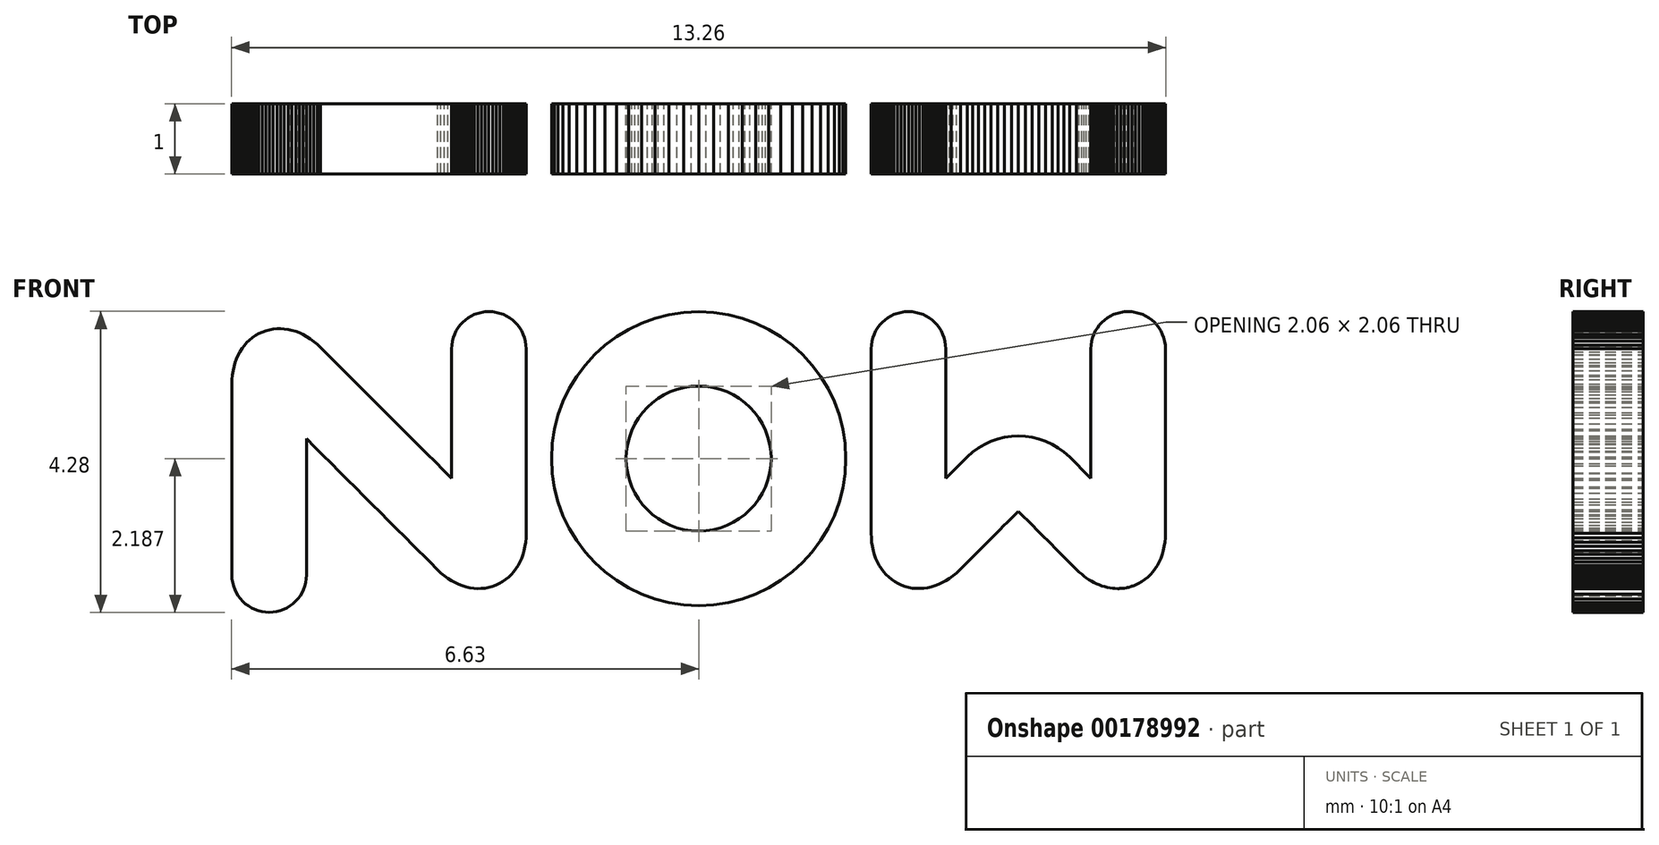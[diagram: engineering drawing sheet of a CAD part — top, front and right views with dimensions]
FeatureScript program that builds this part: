
annotation { "Feature Type Name" : "Feature", "Feature Type Description" : "" }
export const myFeature = defineFeature(function(context is Context, id is Id, definition is map)
    precondition{}
    {
        {
            var Q0;
            Q0=qCreatedBy(makeId("Front.planeOp"),FACE);
            var sketch = newSketch(context, id + "F0", { "sketchPlane" : qUnion([Q0])});
            skLineSegment(sketch, "E0", {"start": v(2.05, 0.47) * mm, "end": v(2, 0.67) * mm});
            skLineSegment(sketch, "E1", {"start": v(2, 0.67) * mm, "end": v(1.92, 0.86) * mm});
            skLineSegment(sketch, "E2", {"start": v(1.92, 0.86) * mm, "end": v(1.84, 1.04) * mm});
            skLineSegment(sketch, "E3", {"start": v(1.84, 1.04) * mm, "end": v(1.73, 1.21) * mm});
            skLineSegment(sketch, "E4", {"start": v(1.73, 1.21) * mm, "end": v(1.61, 1.37) * mm});
            skLineSegment(sketch, "E5", {"start": v(1.61, 1.37) * mm, "end": v(1.48, 1.52) * mm});
            skLineSegment(sketch, "E6", {"start": v(1.48, 1.52) * mm, "end": v(1.33, 1.66) * mm});
            skLineSegment(sketch, "E7", {"start": v(1.33, 1.66) * mm, "end": v(1.17, 1.78) * mm});
            skLineSegment(sketch, "E8", {"start": v(1.17, 1.78) * mm, "end": v(1, 1.88) * mm});
            skLineSegment(sketch, "E9", {"start": v(1, 1.88) * mm, "end": v(0.81, 1.97) * mm});
            skLineSegment(sketch, "E10", {"start": v(0.81, 1.97) * mm, "end": v(0.62, 2.04) * mm});
            skLineSegment(sketch, "E11", {"start": v(0.62, 2.04) * mm, "end": v(0.42, 2.1) * mm});
            skLineSegment(sketch, "E12", {"start": v(0.42, 2.1) * mm, "end": v(0.21, 2.12) * mm});
            skLineSegment(sketch, "E13", {"start": v(0.21, 2.12) * mm, "end": v(0, 2.14) * mm});
            skLineSegment(sketch, "E14", {"start": v(0, 2.14) * mm, "end": v(-0.21, 2.12) * mm});
            skLineSegment(sketch, "E15", {"start": v(-0.21, 2.12) * mm, "end": v(-0.42, 2.1) * mm});
            skLineSegment(sketch, "E16", {"start": v(-0.42, 2.1) * mm, "end": v(-0.62, 2.04) * mm});
            skLineSegment(sketch, "E17", {"start": v(-0.62, 2.04) * mm, "end": v(-0.81, 1.97) * mm});
            skLineSegment(sketch, "E18", {"start": v(-0.81, 1.97) * mm, "end": v(-1, 1.88) * mm});
            skLineSegment(sketch, "E19", {"start": v(-1, 1.88) * mm, "end": v(-1.17, 1.78) * mm});
            skLineSegment(sketch, "E20", {"start": v(-1.17, 1.78) * mm, "end": v(-1.33, 1.66) * mm});
            skLineSegment(sketch, "E21", {"start": v(-1.33, 1.66) * mm, "end": v(-1.48, 1.52) * mm});
            skLineSegment(sketch, "E22", {"start": v(-1.48, 1.52) * mm, "end": v(-1.61, 1.37) * mm});
            skLineSegment(sketch, "E23", {"start": v(-1.61, 1.37) * mm, "end": v(-1.73, 1.21) * mm});
            skLineSegment(sketch, "E24", {"start": v(-1.73, 1.21) * mm, "end": v(-1.84, 1.04) * mm});
            skLineSegment(sketch, "E25", {"start": v(-1.84, 1.04) * mm, "end": v(-1.92, 0.86) * mm});
            skLineSegment(sketch, "E26", {"start": v(-1.92, 0.86) * mm, "end": v(-2, 0.67) * mm});
            skLineSegment(sketch, "E27", {"start": v(-2, 0.67) * mm, "end": v(-2.05, 0.47) * mm});
            skLineSegment(sketch, "E28", {"start": v(-2.05, 0.47) * mm, "end": v(-2.08, 0.26) * mm});
            skLineSegment(sketch, "E29", {"start": v(-2.08, 0.26) * mm, "end": v(-2.09, 0.05) * mm});
            skLineSegment(sketch, "E30", {"start": v(-2.09, 0.05) * mm, "end": v(-2.08, -0.17) * mm});
            skLineSegment(sketch, "E31", {"start": v(-2.08, -0.17) * mm, "end": v(-2.05, -0.37) * mm});
            skLineSegment(sketch, "E32", {"start": v(-2.05, -0.37) * mm, "end": v(-2, -0.57) * mm});
            skLineSegment(sketch, "E33", {"start": v(-2, -0.57) * mm, "end": v(-1.92, -0.76) * mm});
            skLineSegment(sketch, "E34", {"start": v(-1.92, -0.76) * mm, "end": v(-1.84, -0.95) * mm});
            skLineSegment(sketch, "E35", {"start": v(-1.84, -0.95) * mm, "end": v(-1.73, -1.12) * mm});
            skLineSegment(sketch, "E36", {"start": v(-1.73, -1.12) * mm, "end": v(-1.61, -1.28) * mm});
            skLineSegment(sketch, "E37", {"start": v(-1.61, -1.28) * mm, "end": v(-1.48, -1.43) * mm});
            skLineSegment(sketch, "E38", {"start": v(-1.48, -1.43) * mm, "end": v(-1.33, -1.56) * mm});
            skLineSegment(sketch, "E39", {"start": v(-1.33, -1.56) * mm, "end": v(-1.17, -1.68) * mm});
            skLineSegment(sketch, "E40", {"start": v(-1.17, -1.68) * mm, "end": v(-1, -1.79) * mm});
            skLineSegment(sketch, "E41", {"start": v(-1, -1.79) * mm, "end": v(-0.81, -1.88) * mm});
            skLineSegment(sketch, "E42", {"start": v(-0.81, -1.88) * mm, "end": v(-0.62, -1.95) * mm});
            skLineSegment(sketch, "E43", {"start": v(-0.62, -1.95) * mm, "end": v(-0.42, -2) * mm});
            skLineSegment(sketch, "E44", {"start": v(-0.42, -2) * mm, "end": v(-0.21, -2.03) * mm});
            skLineSegment(sketch, "E45", {"start": v(-0.21, -2.03) * mm, "end": v(0, -2.04) * mm});
            skLineSegment(sketch, "E46", {"start": v(0, -2.04) * mm, "end": v(0.21, -2.03) * mm});
            skLineSegment(sketch, "E47", {"start": v(0.21, -2.03) * mm, "end": v(0.42, -2) * mm});
            skLineSegment(sketch, "E48", {"start": v(0.42, -2) * mm, "end": v(0.62, -1.95) * mm});
            skLineSegment(sketch, "E49", {"start": v(0.62, -1.95) * mm, "end": v(0.81, -1.88) * mm});
            skLineSegment(sketch, "E50", {"start": v(0.81, -1.88) * mm, "end": v(1, -1.79) * mm});
            skLineSegment(sketch, "E51", {"start": v(1, -1.79) * mm, "end": v(1.17, -1.68) * mm});
            skLineSegment(sketch, "E52", {"start": v(1.17, -1.68) * mm, "end": v(1.33, -1.56) * mm});
            skLineSegment(sketch, "E53", {"start": v(1.33, -1.56) * mm, "end": v(1.48, -1.43) * mm});
            skLineSegment(sketch, "E54", {"start": v(1.48, -1.43) * mm, "end": v(1.61, -1.28) * mm});
            skLineSegment(sketch, "E55", {"start": v(1.61, -1.28) * mm, "end": v(1.73, -1.12) * mm});
            skLineSegment(sketch, "E56", {"start": v(1.73, -1.12) * mm, "end": v(1.84, -0.95) * mm});
            skLineSegment(sketch, "E57", {"start": v(1.84, -0.95) * mm, "end": v(1.92, -0.76) * mm});
            skLineSegment(sketch, "E58", {"start": v(1.92, -0.76) * mm, "end": v(2, -0.57) * mm});
            skLineSegment(sketch, "E59", {"start": v(2, -0.57) * mm, "end": v(2.05, -0.37) * mm});
            skLineSegment(sketch, "E60", {"start": v(2.05, -0.37) * mm, "end": v(2.08, -0.17) * mm});
            skLineSegment(sketch, "E61", {"start": v(2.08, -0.17) * mm, "end": v(2.09, 0.05) * mm});
            skLineSegment(sketch, "E62", {"start": v(2.09, 0.05) * mm, "end": v(2.08, 0.26) * mm});
            skLineSegment(sketch, "E63", {"start": v(2.08, 0.26) * mm, "end": v(2.05, 0.47) * mm});
            skLineSegment(sketch, "E64", {"start": v(1.02, -0.06) * mm, "end": v(1, -0.16) * mm});
            skLineSegment(sketch, "E65", {"start": v(1, -0.16) * mm, "end": v(0.98, -0.26) * mm});
            skLineSegment(sketch, "E66", {"start": v(0.98, -0.26) * mm, "end": v(0.95, -0.35) * mm});
            skLineSegment(sketch, "E67", {"start": v(0.95, -0.35) * mm, "end": v(0.9, -0.44) * mm});
            skLineSegment(sketch, "E68", {"start": v(0.9, -0.44) * mm, "end": v(0.85, -0.53) * mm});
            skLineSegment(sketch, "E69", {"start": v(0.85, -0.53) * mm, "end": v(0.8, -0.6) * mm});
            skLineSegment(sketch, "E70", {"start": v(0.8, -0.6) * mm, "end": v(0.73, -0.68) * mm});
            skLineSegment(sketch, "E71", {"start": v(0.73, -0.68) * mm, "end": v(0.65, -0.75) * mm});
            skLineSegment(sketch, "E72", {"start": v(0.65, -0.75) * mm, "end": v(0.58, -0.8) * mm});
            skLineSegment(sketch, "E73", {"start": v(0.58, -0.8) * mm, "end": v(0.5, -0.86) * mm});
            skLineSegment(sketch, "E74", {"start": v(0.5, -0.86) * mm, "end": v(0.4, -0.9) * mm});
            skLineSegment(sketch, "E75", {"start": v(0.4, -0.9) * mm, "end": v(0.3, -0.94) * mm});
            skLineSegment(sketch, "E76", {"start": v(0.3, -0.94) * mm, "end": v(0.2, -0.96) * mm});
            skLineSegment(sketch, "E77", {"start": v(0.2, -0.96) * mm, "end": v(0.1, -0.98) * mm});
            skLineSegment(sketch, "E78", {"start": v(0.1, -0.98) * mm, "end": v(0, -0.98) * mm});
            skLineSegment(sketch, "E79", {"start": v(0, -0.98) * mm, "end": v(-0.1, -0.98) * mm});
            skLineSegment(sketch, "E80", {"start": v(-0.1, -0.98) * mm, "end": v(-0.2, -0.96) * mm});
            skLineSegment(sketch, "E81", {"start": v(-0.2, -0.96) * mm, "end": v(-0.3, -0.94) * mm});
            skLineSegment(sketch, "E82", {"start": v(-0.3, -0.94) * mm, "end": v(-0.4, -0.9) * mm});
            skLineSegment(sketch, "E83", {"start": v(-0.4, -0.9) * mm, "end": v(-0.5, -0.86) * mm});
            skLineSegment(sketch, "E84", {"start": v(-0.5, -0.86) * mm, "end": v(-0.58, -0.8) * mm});
            skLineSegment(sketch, "E85", {"start": v(-0.58, -0.8) * mm, "end": v(-0.65, -0.75) * mm});
            skLineSegment(sketch, "E86", {"start": v(-0.65, -0.75) * mm, "end": v(-0.73, -0.68) * mm});
            skLineSegment(sketch, "E87", {"start": v(-0.73, -0.68) * mm, "end": v(-0.8, -0.6) * mm});
            skLineSegment(sketch, "E88", {"start": v(-0.8, -0.6) * mm, "end": v(-0.85, -0.53) * mm});
            skLineSegment(sketch, "E89", {"start": v(-0.85, -0.53) * mm, "end": v(-0.9, -0.44) * mm});
            skLineSegment(sketch, "E90", {"start": v(-0.9, -0.44) * mm, "end": v(-0.95, -0.35) * mm});
            skLineSegment(sketch, "E91", {"start": v(-0.95, -0.35) * mm, "end": v(-0.98, -0.26) * mm});
            skLineSegment(sketch, "E92", {"start": v(-0.98, -0.26) * mm, "end": v(-1, -0.16) * mm});
            skLineSegment(sketch, "E93", {"start": v(-1, -0.16) * mm, "end": v(-1.02, -0.06) * mm});
            skLineSegment(sketch, "E94", {"start": v(-1.02, -0.06) * mm, "end": v(-1.03, 0.05) * mm});
            skLineSegment(sketch, "E95", {"start": v(-1.03, 0.05) * mm, "end": v(-1.02, 0.15) * mm});
            skLineSegment(sketch, "E96", {"start": v(-1.02, 0.15) * mm, "end": v(-1, 0.25) * mm});
            skLineSegment(sketch, "E97", {"start": v(-1, 0.25) * mm, "end": v(-0.98, 0.35) * mm});
            skLineSegment(sketch, "E98", {"start": v(-0.98, 0.35) * mm, "end": v(-0.95, 0.45) * mm});
            skLineSegment(sketch, "E99", {"start": v(-0.95, 0.45) * mm, "end": v(-0.9, 0.54) * mm});
            skLineSegment(sketch, "E100", {"start": v(-0.9, 0.54) * mm, "end": v(-0.85, 0.62) * mm});
            skLineSegment(sketch, "E101", {"start": v(-0.85, 0.62) * mm, "end": v(-0.8, 0.7) * mm});
            skLineSegment(sketch, "E102", {"start": v(-0.8, 0.7) * mm, "end": v(-0.73, 0.78) * mm});
            skLineSegment(sketch, "E103", {"start": v(-0.73, 0.78) * mm, "end": v(-0.65, 0.84) * mm});
            skLineSegment(sketch, "E104", {"start": v(-0.65, 0.84) * mm, "end": v(-0.58, 0.9) * mm});
            skLineSegment(sketch, "E105", {"start": v(-0.58, 0.9) * mm, "end": v(-0.5, 0.95) * mm});
            skLineSegment(sketch, "E106", {"start": v(-0.5, 0.95) * mm, "end": v(-0.4, 1) * mm});
            skLineSegment(sketch, "E107", {"start": v(-0.4, 1) * mm, "end": v(-0.3, 1.03) * mm});
            skLineSegment(sketch, "E108", {"start": v(-0.3, 1.03) * mm, "end": v(-0.2, 1.06) * mm});
            skLineSegment(sketch, "E109", {"start": v(-0.2, 1.06) * mm, "end": v(-0.1, 1.07) * mm});
            skLineSegment(sketch, "E110", {"start": v(-0.1, 1.07) * mm, "end": v(0, 1.08) * mm});
            skLineSegment(sketch, "E111", {"start": v(0, 1.08) * mm, "end": v(0.1, 1.07) * mm});
            skLineSegment(sketch, "E112", {"start": v(0.1, 1.07) * mm, "end": v(0.2, 1.06) * mm});
            skLineSegment(sketch, "E113", {"start": v(0.2, 1.06) * mm, "end": v(0.3, 1.03) * mm});
            skLineSegment(sketch, "E114", {"start": v(0.3, 1.03) * mm, "end": v(0.4, 1) * mm});
            skLineSegment(sketch, "E115", {"start": v(0.4, 1) * mm, "end": v(0.5, 0.95) * mm});
            skLineSegment(sketch, "E116", {"start": v(0.5, 0.95) * mm, "end": v(0.58, 0.9) * mm});
            skLineSegment(sketch, "E117", {"start": v(0.58, 0.9) * mm, "end": v(0.65, 0.84) * mm});
            skLineSegment(sketch, "E118", {"start": v(0.65, 0.84) * mm, "end": v(0.73, 0.78) * mm});
            skLineSegment(sketch, "E119", {"start": v(0.73, 0.78) * mm, "end": v(0.8, 0.7) * mm});
            skLineSegment(sketch, "E120", {"start": v(0.8, 0.7) * mm, "end": v(0.85, 0.62) * mm});
            skLineSegment(sketch, "E121", {"start": v(0.85, 0.62) * mm, "end": v(0.9, 0.54) * mm});
            skLineSegment(sketch, "E122", {"start": v(0.9, 0.54) * mm, "end": v(0.95, 0.45) * mm});
            skLineSegment(sketch, "E123", {"start": v(0.95, 0.45) * mm, "end": v(0.98, 0.35) * mm});
            skLineSegment(sketch, "E124", {"start": v(0.98, 0.35) * mm, "end": v(1, 0.25) * mm});
            skLineSegment(sketch, "E125", {"start": v(1, 0.25) * mm, "end": v(1.02, 0.15) * mm});
            skLineSegment(sketch, "E126", {"start": v(1.02, 0.15) * mm, "end": v(1.03, 0.05) * mm});
            skLineSegment(sketch, "E127", {"start": v(1.03, 0.05) * mm, "end": v(1.02, -0.06) * mm});
            skLineSegment(sketch, "E128", {"start": v(-2.46, 1.71) * mm, "end": v(-2.47, 1.76) * mm});
            skLineSegment(sketch, "E129", {"start": v(-2.47, 1.76) * mm, "end": v(-2.5, 1.81) * mm});
            skLineSegment(sketch, "E130", {"start": v(-2.5, 1.81) * mm, "end": v(-2.51, 1.86) * mm});
            skLineSegment(sketch, "E131", {"start": v(-2.51, 1.86) * mm, "end": v(-2.54, 1.9) * mm});
            skLineSegment(sketch, "E132", {"start": v(-2.54, 1.9) * mm, "end": v(-2.57, 1.94) * mm});
            skLineSegment(sketch, "E133", {"start": v(-2.57, 1.94) * mm, "end": v(-2.6, 1.98) * mm});
            skLineSegment(sketch, "E134", {"start": v(-2.6, 1.98) * mm, "end": v(-2.64, 2.01) * mm});
            skLineSegment(sketch, "E135", {"start": v(-2.64, 2.01) * mm, "end": v(-2.68, 2.05) * mm});
            skLineSegment(sketch, "E136", {"start": v(-2.68, 2.05) * mm, "end": v(-2.73, 2.07) * mm});
            skLineSegment(sketch, "E137", {"start": v(-2.73, 2.07) * mm, "end": v(-2.77, 2.1) * mm});
            skLineSegment(sketch, "E138", {"start": v(-2.77, 2.1) * mm, "end": v(-2.82, 2.11) * mm});
            skLineSegment(sketch, "E139", {"start": v(-2.82, 2.11) * mm, "end": v(-2.87, 2.13) * mm});
            skLineSegment(sketch, "E140", {"start": v(-2.87, 2.13) * mm, "end": v(-2.92, 2.13) * mm});
            skLineSegment(sketch, "E141", {"start": v(-2.92, 2.13) * mm, "end": v(-2.98, 2.14) * mm});
            skLineSegment(sketch, "E142", {"start": v(-2.98, 2.14) * mm, "end": v(-3.03, 2.13) * mm});
            skLineSegment(sketch, "E143", {"start": v(-3.03, 2.13) * mm, "end": v(-3.08, 2.13) * mm});
            skLineSegment(sketch, "E144", {"start": v(-3.08, 2.13) * mm, "end": v(-3.14, 2.11) * mm});
            skLineSegment(sketch, "E145", {"start": v(-3.14, 2.11) * mm, "end": v(-3.18, 2.1) * mm});
            skLineSegment(sketch, "E146", {"start": v(-3.18, 2.1) * mm, "end": v(-3.23, 2.07) * mm});
            skLineSegment(sketch, "E147", {"start": v(-3.23, 2.07) * mm, "end": v(-3.27, 2.05) * mm});
            skLineSegment(sketch, "E148", {"start": v(-3.27, 2.05) * mm, "end": v(-3.31, 2.01) * mm});
            skLineSegment(sketch, "E149", {"start": v(-3.31, 2.01) * mm, "end": v(-3.35, 1.98) * mm});
            skLineSegment(sketch, "E150", {"start": v(-3.35, 1.98) * mm, "end": v(-3.39, 1.94) * mm});
            skLineSegment(sketch, "E151", {"start": v(-3.39, 1.94) * mm, "end": v(-3.42, 1.9) * mm});
            skLineSegment(sketch, "E152", {"start": v(-3.42, 1.9) * mm, "end": v(-3.44, 1.86) * mm});
            skLineSegment(sketch, "E153", {"start": v(-3.44, 1.86) * mm, "end": v(-3.47, 1.81) * mm});
            skLineSegment(sketch, "E154", {"start": v(-3.47, 1.81) * mm, "end": v(-3.48, 1.76) * mm});
            skLineSegment(sketch, "E155", {"start": v(-3.48, 1.76) * mm, "end": v(-3.5, 1.71) * mm});
            skLineSegment(sketch, "E156", {"start": v(-3.5, 1.71) * mm, "end": v(-3.5, 1.66) * mm});
            skLineSegment(sketch, "E157", {"start": v(-3.5, 1.66) * mm, "end": v(-3.5, 1.6) * mm});
            skLineSegment(sketch, "E158", {"start": v(-3.5, 1.6) * mm, "end": v(-3.5, 1.5) * mm});
            skLineSegment(sketch, "E159", {"start": v(-3.5, 1.5) * mm, "end": v(-3.5, 1.38) * mm});
            skLineSegment(sketch, "E160", {"start": v(-3.5, 1.38) * mm, "end": v(-3.5, 1.26) * mm});
            skLineSegment(sketch, "E161", {"start": v(-3.5, 1.26) * mm, "end": v(-3.5, 1.15) * mm});
            skLineSegment(sketch, "E162", {"start": v(-3.5, 1.15) * mm, "end": v(-3.5, 1.03) * mm});
            skLineSegment(sketch, "E163", {"start": v(-3.5, 1.03) * mm, "end": v(-3.5, 0.92) * mm});
            skLineSegment(sketch, "E164", {"start": v(-3.5, 0.92) * mm, "end": v(-3.5, 0.8) * mm});
            skLineSegment(sketch, "E165", {"start": v(-3.5, 0.8) * mm, "end": v(-3.5, 0.69) * mm});
            skLineSegment(sketch, "E166", {"start": v(-3.5, 0.69) * mm, "end": v(-3.5, 0.57) * mm});
            skLineSegment(sketch, "E167", {"start": v(-3.5, 0.57) * mm, "end": v(-3.5, 0.46) * mm});
            skLineSegment(sketch, "E168", {"start": v(-3.5, 0.46) * mm, "end": v(-3.5, 0.34) * mm});
            skLineSegment(sketch, "E169", {"start": v(-3.5, 0.34) * mm, "end": v(-3.5, 0.23) * mm});
            skLineSegment(sketch, "E170", {"start": v(-3.5, 0.23) * mm, "end": v(-3.5, 0.11) * mm});
            skLineSegment(sketch, "E171", {"start": v(-3.5, 0.11) * mm, "end": v(-3.5, 0) * mm});
            skLineSegment(sketch, "E172", {"start": v(-3.5, 0) * mm, "end": v(-3.5, -0.12) * mm});
            skLineSegment(sketch, "E173", {"start": v(-3.5, -0.12) * mm, "end": v(-3.5, -0.23) * mm});
            skLineSegment(sketch, "E174", {"start": v(-3.5, -0.23) * mm, "end": v(-3.62, -0.12) * mm});
            skLineSegment(sketch, "E175", {"start": v(-3.62, -0.12) * mm, "end": v(-3.74, 0) * mm});
            skLineSegment(sketch, "E176", {"start": v(-3.74, 0) * mm, "end": v(-3.86, 0.11) * mm});
            skLineSegment(sketch, "E177", {"start": v(-3.86, 0.11) * mm, "end": v(-3.97, 0.23) * mm});
            skLineSegment(sketch, "E178", {"start": v(-3.97, 0.23) * mm, "end": v(-4.09, 0.35) * mm});
            skLineSegment(sketch, "E179", {"start": v(-4.09, 0.35) * mm, "end": v(-4.2, 0.46) * mm});
            skLineSegment(sketch, "E180", {"start": v(-4.2, 0.46) * mm, "end": v(-4.32, 0.58) * mm});
            skLineSegment(sketch, "E181", {"start": v(-4.32, 0.58) * mm, "end": v(-4.44, 0.7) * mm});
            skLineSegment(sketch, "E182", {"start": v(-4.44, 0.7) * mm, "end": v(-4.55, 0.81) * mm});
            skLineSegment(sketch, "E183", {"start": v(-4.55, 0.81) * mm, "end": v(-4.67, 0.93) * mm});
            skLineSegment(sketch, "E184", {"start": v(-4.67, 0.93) * mm, "end": v(-4.79, 1.05) * mm});
            skLineSegment(sketch, "E185", {"start": v(-4.79, 1.05) * mm, "end": v(-4.9, 1.16) * mm});
            skLineSegment(sketch, "E186", {"start": v(-4.9, 1.16) * mm, "end": v(-5.02, 1.28) * mm});
            skLineSegment(sketch, "E187", {"start": v(-5.02, 1.28) * mm, "end": v(-5.14, 1.4) * mm});
            skLineSegment(sketch, "E188", {"start": v(-5.14, 1.4) * mm, "end": v(-5.25, 1.51) * mm});
            skLineSegment(sketch, "E189", {"start": v(-5.25, 1.51) * mm, "end": v(-5.37, 1.63) * mm});
            skLineSegment(sketch, "E190", {"start": v(-5.37, 1.63) * mm, "end": v(-5.42, 1.67) * mm});
            skLineSegment(sketch, "E191", {"start": v(-5.42, 1.67) * mm, "end": v(-5.46, 1.71) * mm});
            skLineSegment(sketch, "E192", {"start": v(-5.46, 1.71) * mm, "end": v(-5.51, 1.75) * mm});
            skLineSegment(sketch, "E193", {"start": v(-5.51, 1.75) * mm, "end": v(-5.56, 1.78) * mm});
            skLineSegment(sketch, "E194", {"start": v(-5.56, 1.78) * mm, "end": v(-5.62, 1.8) * mm});
            skLineSegment(sketch, "E195", {"start": v(-5.62, 1.8) * mm, "end": v(-5.67, 1.83) * mm});
            skLineSegment(sketch, "E196", {"start": v(-5.67, 1.83) * mm, "end": v(-5.72, 1.85) * mm});
            skLineSegment(sketch, "E197", {"start": v(-5.72, 1.85) * mm, "end": v(-5.77, 1.87) * mm});
            skLineSegment(sketch, "E198", {"start": v(-5.77, 1.87) * mm, "end": v(-5.83, 1.88) * mm});
            skLineSegment(sketch, "E199", {"start": v(-5.83, 1.88) * mm, "end": v(-5.88, 1.9) * mm});
            skLineSegment(sketch, "E200", {"start": v(-5.88, 1.9) * mm, "end": v(-5.93, 1.9) * mm});
            skLineSegment(sketch, "E201", {"start": v(-5.93, 1.9) * mm, "end": v(-5.99, 1.9) * mm});
            skLineSegment(sketch, "E202", {"start": v(-5.99, 1.9) * mm, "end": v(-6.04, 1.89) * mm});
            skLineSegment(sketch, "E203", {"start": v(-6.04, 1.89) * mm, "end": v(-6.1, 1.88) * mm});
            skLineSegment(sketch, "E204", {"start": v(-6.1, 1.88) * mm, "end": v(-6.14, 1.86) * mm});
            skLineSegment(sketch, "E205", {"start": v(-6.14, 1.86) * mm, "end": v(-6.2, 1.84) * mm});
            skLineSegment(sketch, "E206", {"start": v(-6.2, 1.84) * mm, "end": v(-6.24, 1.82) * mm});
            skLineSegment(sketch, "E207", {"start": v(-6.24, 1.82) * mm, "end": v(-6.3, 1.8) * mm});
            skLineSegment(sketch, "E208", {"start": v(-6.3, 1.8) * mm, "end": v(-6.34, 1.77) * mm});
            skLineSegment(sketch, "E209", {"start": v(-6.34, 1.77) * mm, "end": v(-6.38, 1.73) * mm});
            skLineSegment(sketch, "E210", {"start": v(-6.38, 1.73) * mm, "end": v(-6.41, 1.7) * mm});
            skLineSegment(sketch, "E211", {"start": v(-6.41, 1.7) * mm, "end": v(-6.45, 1.65) * mm});
            skLineSegment(sketch, "E212", {"start": v(-6.45, 1.65) * mm, "end": v(-6.48, 1.61) * mm});
            skLineSegment(sketch, "E213", {"start": v(-6.48, 1.61) * mm, "end": v(-6.51, 1.57) * mm});
            skLineSegment(sketch, "E214", {"start": v(-6.51, 1.57) * mm, "end": v(-6.54, 1.52) * mm});
            skLineSegment(sketch, "E215", {"start": v(-6.54, 1.52) * mm, "end": v(-6.56, 1.46) * mm});
            skLineSegment(sketch, "E216", {"start": v(-6.56, 1.46) * mm, "end": v(-6.58, 1.41) * mm});
            skLineSegment(sketch, "E217", {"start": v(-6.58, 1.41) * mm, "end": v(-6.6, 1.35) * mm});
            skLineSegment(sketch, "E218", {"start": v(-6.6, 1.35) * mm, "end": v(-6.6, 1.3) * mm});
            skLineSegment(sketch, "E219", {"start": v(-6.6, 1.3) * mm, "end": v(-6.62, 1.23) * mm});
            skLineSegment(sketch, "E220", {"start": v(-6.62, 1.23) * mm, "end": v(-6.62, 1.17) * mm});
            skLineSegment(sketch, "E221", {"start": v(-6.62, 1.17) * mm, "end": v(-6.63, 1.1) * mm});
            skLineSegment(sketch, "E222", {"start": v(-6.63, 1.1) * mm, "end": v(-6.63, 0.94) * mm});
            skLineSegment(sketch, "E223", {"start": v(-6.63, 0.94) * mm, "end": v(-6.63, 0.77) * mm});
            skLineSegment(sketch, "E224", {"start": v(-6.63, 0.77) * mm, "end": v(-6.63, 0.6) * mm});
            skLineSegment(sketch, "E225", {"start": v(-6.63, 0.6) * mm, "end": v(-6.63, 0.43) * mm});
            skLineSegment(sketch, "E226", {"start": v(-6.63, 0.43) * mm, "end": v(-6.63, 0.26) * mm});
            skLineSegment(sketch, "E227", {"start": v(-6.63, 0.26) * mm, "end": v(-6.63, 0.09) * mm});
            skLineSegment(sketch, "E228", {"start": v(-6.63, 0.09) * mm, "end": v(-6.63, -0.08) * mm});
            skLineSegment(sketch, "E229", {"start": v(-6.63, -0.08) * mm, "end": v(-6.63, -0.25) * mm});
            skLineSegment(sketch, "E230", {"start": v(-6.63, -0.25) * mm, "end": v(-6.63, -0.42) * mm});
            skLineSegment(sketch, "E231", {"start": v(-6.63, -0.42) * mm, "end": v(-6.63, -0.59) * mm});
            skLineSegment(sketch, "E232", {"start": v(-6.63, -0.59) * mm, "end": v(-6.63, -0.76) * mm});
            skLineSegment(sketch, "E233", {"start": v(-6.63, -0.76) * mm, "end": v(-6.63, -0.93) * mm});
            skLineSegment(sketch, "E234", {"start": v(-6.63, -0.93) * mm, "end": v(-6.63, -1.1) * mm});
            skLineSegment(sketch, "E235", {"start": v(-6.63, -1.1) * mm, "end": v(-6.63, -1.27) * mm});
            skLineSegment(sketch, "E236", {"start": v(-6.63, -1.27) * mm, "end": v(-6.63, -1.44) * mm});
            skLineSegment(sketch, "E237", {"start": v(-6.63, -1.44) * mm, "end": v(-6.63, -1.6) * mm});
            skLineSegment(sketch, "E238", {"start": v(-6.63, -1.6) * mm, "end": v(-6.62, -1.66) * mm});
            skLineSegment(sketch, "E239", {"start": v(-6.62, -1.66) * mm, "end": v(-6.62, -1.71) * mm});
            skLineSegment(sketch, "E240", {"start": v(-6.62, -1.71) * mm, "end": v(-6.6, -1.76) * mm});
            skLineSegment(sketch, "E241", {"start": v(-6.6, -1.76) * mm, "end": v(-6.58, -1.81) * mm});
            skLineSegment(sketch, "E242", {"start": v(-6.58, -1.81) * mm, "end": v(-6.56, -1.86) * mm});
            skLineSegment(sketch, "E243", {"start": v(-6.56, -1.86) * mm, "end": v(-6.54, -1.9) * mm});
            skLineSegment(sketch, "E244", {"start": v(-6.54, -1.9) * mm, "end": v(-6.5, -1.94) * mm});
            skLineSegment(sketch, "E245", {"start": v(-6.5, -1.94) * mm, "end": v(-6.47, -1.98) * mm});
            skLineSegment(sketch, "E246", {"start": v(-6.47, -1.98) * mm, "end": v(-6.43, -2.02) * mm});
            skLineSegment(sketch, "E247", {"start": v(-6.43, -2.02) * mm, "end": v(-6.4, -2.05) * mm});
            skLineSegment(sketch, "E248", {"start": v(-6.4, -2.05) * mm, "end": v(-6.35, -2.07) * mm});
            skLineSegment(sketch, "E249", {"start": v(-6.35, -2.07) * mm, "end": v(-6.3, -2.1) * mm});
            skLineSegment(sketch, "E250", {"start": v(-6.3, -2.1) * mm, "end": v(-6.25, -2.11) * mm});
            skLineSegment(sketch, "E251", {"start": v(-6.25, -2.11) * mm, "end": v(-6.2, -2.13) * mm});
            skLineSegment(sketch, "E252", {"start": v(-6.2, -2.13) * mm, "end": v(-6.15, -2.13) * mm});
            skLineSegment(sketch, "E253", {"start": v(-6.15, -2.13) * mm, "end": v(-6.1, -2.14) * mm});
            skLineSegment(sketch, "E254", {"start": v(-6.1, -2.14) * mm, "end": v(-6.04, -2.13) * mm});
            skLineSegment(sketch, "E255", {"start": v(-6.04, -2.13) * mm, "end": v(-6, -2.13) * mm});
            skLineSegment(sketch, "E256", {"start": v(-6, -2.13) * mm, "end": v(-5.94, -2.11) * mm});
            skLineSegment(sketch, "E257", {"start": v(-5.94, -2.11) * mm, "end": v(-5.9, -2.1) * mm});
            skLineSegment(sketch, "E258", {"start": v(-5.9, -2.1) * mm, "end": v(-5.84, -2.07) * mm});
            skLineSegment(sketch, "E259", {"start": v(-5.84, -2.07) * mm, "end": v(-5.8, -2.05) * mm});
            skLineSegment(sketch, "E260", {"start": v(-5.8, -2.05) * mm, "end": v(-5.76, -2.02) * mm});
            skLineSegment(sketch, "E261", {"start": v(-5.76, -2.02) * mm, "end": v(-5.72, -1.98) * mm});
            skLineSegment(sketch, "E262", {"start": v(-5.72, -1.98) * mm, "end": v(-5.69, -1.94) * mm});
            skLineSegment(sketch, "E263", {"start": v(-5.69, -1.94) * mm, "end": v(-5.66, -1.9) * mm});
            skLineSegment(sketch, "E264", {"start": v(-5.66, -1.9) * mm, "end": v(-5.63, -1.86) * mm});
            skLineSegment(sketch, "E265", {"start": v(-5.63, -1.86) * mm, "end": v(-5.6, -1.81) * mm});
            skLineSegment(sketch, "E266", {"start": v(-5.6, -1.81) * mm, "end": v(-5.6, -1.76) * mm});
            skLineSegment(sketch, "E267", {"start": v(-5.6, -1.76) * mm, "end": v(-5.58, -1.71) * mm});
            skLineSegment(sketch, "E268", {"start": v(-5.58, -1.71) * mm, "end": v(-5.57, -1.66) * mm});
            skLineSegment(sketch, "E269", {"start": v(-5.57, -1.66) * mm, "end": v(-5.57, -1.6) * mm});
            skLineSegment(sketch, "E270", {"start": v(-5.57, -1.6) * mm, "end": v(-5.57, -1.49) * mm});
            skLineSegment(sketch, "E271", {"start": v(-5.57, -1.49) * mm, "end": v(-5.57, -1.36) * mm});
            skLineSegment(sketch, "E272", {"start": v(-5.57, -1.36) * mm, "end": v(-5.57, -1.24) * mm});
            skLineSegment(sketch, "E273", {"start": v(-5.57, -1.24) * mm, "end": v(-5.57, -1.12) * mm});
            skLineSegment(sketch, "E274", {"start": v(-5.57, -1.12) * mm, "end": v(-5.57, -1) * mm});
            skLineSegment(sketch, "E275", {"start": v(-5.57, -1) * mm, "end": v(-5.57, -0.88) * mm});
            skLineSegment(sketch, "E276", {"start": v(-5.57, -0.88) * mm, "end": v(-5.57, -0.76) * mm});
            skLineSegment(sketch, "E277", {"start": v(-5.57, -0.76) * mm, "end": v(-5.57, -0.64) * mm});
            skLineSegment(sketch, "E278", {"start": v(-5.57, -0.64) * mm, "end": v(-5.57, -0.52) * mm});
            skLineSegment(sketch, "E279", {"start": v(-5.57, -0.52) * mm, "end": v(-5.57, -0.4) * mm});
            skLineSegment(sketch, "E280", {"start": v(-5.57, -0.4) * mm, "end": v(-5.57, -0.28) * mm});
            skLineSegment(sketch, "E281", {"start": v(-5.57, -0.28) * mm, "end": v(-5.57, -0.15) * mm});
            skLineSegment(sketch, "E282", {"start": v(-5.57, -0.15) * mm, "end": v(-5.57, -0.03) * mm});
            skLineSegment(sketch, "E283", {"start": v(-5.57, -0.03) * mm, "end": v(-5.57, 0.09) * mm});
            skLineSegment(sketch, "E284", {"start": v(-5.57, 0.09) * mm, "end": v(-5.57, 0.2) * mm});
            skLineSegment(sketch, "E285", {"start": v(-5.57, 0.2) * mm, "end": v(-5.57, 0.33) * mm});
            skLineSegment(sketch, "E286", {"start": v(-5.57, 0.33) * mm, "end": v(-5.45, 0.21) * mm});
            skLineSegment(sketch, "E287", {"start": v(-5.45, 0.21) * mm, "end": v(-5.33, 0.1) * mm});
            skLineSegment(sketch, "E288", {"start": v(-5.33, 0.1) * mm, "end": v(-5.22, -0.02) * mm});
            skLineSegment(sketch, "E289", {"start": v(-5.22, -0.02) * mm, "end": v(-5.1, -0.14) * mm});
            skLineSegment(sketch, "E290", {"start": v(-5.1, -0.14) * mm, "end": v(-4.99, -0.25) * mm});
            skLineSegment(sketch, "E291", {"start": v(-4.99, -0.25) * mm, "end": v(-4.87, -0.37) * mm});
            skLineSegment(sketch, "E292", {"start": v(-4.87, -0.37) * mm, "end": v(-4.75, -0.49) * mm});
            skLineSegment(sketch, "E293", {"start": v(-4.75, -0.49) * mm, "end": v(-4.64, -0.6) * mm});
            skLineSegment(sketch, "E294", {"start": v(-4.64, -0.6) * mm, "end": v(-4.52, -0.72) * mm});
            skLineSegment(sketch, "E295", {"start": v(-4.52, -0.72) * mm, "end": v(-4.4, -0.83) * mm});
            skLineSegment(sketch, "E296", {"start": v(-4.4, -0.83) * mm, "end": v(-4.29, -0.95) * mm});
            skLineSegment(sketch, "E297", {"start": v(-4.29, -0.95) * mm, "end": v(-4.17, -1.07) * mm});
            skLineSegment(sketch, "E298", {"start": v(-4.17, -1.07) * mm, "end": v(-4.05, -1.18) * mm});
            skLineSegment(sketch, "E299", {"start": v(-4.05, -1.18) * mm, "end": v(-3.94, -1.3) * mm});
            skLineSegment(sketch, "E300", {"start": v(-3.94, -1.3) * mm, "end": v(-3.82, -1.42) * mm});
            skLineSegment(sketch, "E301", {"start": v(-3.82, -1.42) * mm, "end": v(-3.7, -1.53) * mm});
            skLineSegment(sketch, "E302", {"start": v(-3.7, -1.53) * mm, "end": v(-3.66, -1.58) * mm});
            skLineSegment(sketch, "E303", {"start": v(-3.66, -1.58) * mm, "end": v(-3.61, -1.62) * mm});
            skLineSegment(sketch, "E304", {"start": v(-3.61, -1.62) * mm, "end": v(-3.56, -1.65) * mm});
            skLineSegment(sketch, "E305", {"start": v(-3.56, -1.65) * mm, "end": v(-3.51, -1.69) * mm});
            skLineSegment(sketch, "E306", {"start": v(-3.51, -1.69) * mm, "end": v(-3.46, -1.72) * mm});
            skLineSegment(sketch, "E307", {"start": v(-3.46, -1.72) * mm, "end": v(-3.4, -1.74) * mm});
            skLineSegment(sketch, "E308", {"start": v(-3.4, -1.74) * mm, "end": v(-3.35, -1.76) * mm});
            skLineSegment(sketch, "E309", {"start": v(-3.35, -1.76) * mm, "end": v(-3.3, -1.78) * mm});
            skLineSegment(sketch, "E310", {"start": v(-3.3, -1.78) * mm, "end": v(-3.25, -1.79) * mm});
            skLineSegment(sketch, "E311", {"start": v(-3.25, -1.79) * mm, "end": v(-3.2, -1.8) * mm});
            skLineSegment(sketch, "E312", {"start": v(-3.2, -1.8) * mm, "end": v(-3.14, -1.8) * mm});
            skLineSegment(sketch, "E313", {"start": v(-3.14, -1.8) * mm, "end": v(-3.09, -1.8) * mm});
            skLineSegment(sketch, "E314", {"start": v(-3.09, -1.8) * mm, "end": v(-3.03, -1.8) * mm});
            skLineSegment(sketch, "E315", {"start": v(-3.03, -1.8) * mm, "end": v(-2.98, -1.78) * mm});
            skLineSegment(sketch, "E316", {"start": v(-2.98, -1.78) * mm, "end": v(-2.93, -1.77) * mm});
            skLineSegment(sketch, "E317", {"start": v(-2.93, -1.77) * mm, "end": v(-2.88, -1.75) * mm});
            skLineSegment(sketch, "E318", {"start": v(-2.88, -1.75) * mm, "end": v(-2.83, -1.73) * mm});
            skLineSegment(sketch, "E319", {"start": v(-2.83, -1.73) * mm, "end": v(-2.78, -1.7) * mm});
            skLineSegment(sketch, "E320", {"start": v(-2.78, -1.7) * mm, "end": v(-2.74, -1.67) * mm});
            skLineSegment(sketch, "E321", {"start": v(-2.74, -1.67) * mm, "end": v(-2.7, -1.64) * mm});
            skLineSegment(sketch, "E322", {"start": v(-2.7, -1.64) * mm, "end": v(-2.66, -1.6) * mm});
            skLineSegment(sketch, "E323", {"start": v(-2.66, -1.6) * mm, "end": v(-2.62, -1.56) * mm});
            skLineSegment(sketch, "E324", {"start": v(-2.62, -1.56) * mm, "end": v(-2.6, -1.52) * mm});
            skLineSegment(sketch, "E325", {"start": v(-2.6, -1.52) * mm, "end": v(-2.56, -1.47) * mm});
            skLineSegment(sketch, "E326", {"start": v(-2.56, -1.47) * mm, "end": v(-2.54, -1.42) * mm});
            skLineSegment(sketch, "E327", {"start": v(-2.54, -1.42) * mm, "end": v(-2.51, -1.37) * mm});
            skLineSegment(sketch, "E328", {"start": v(-2.51, -1.37) * mm, "end": v(-2.5, -1.32) * mm});
            skLineSegment(sketch, "E329", {"start": v(-2.5, -1.32) * mm, "end": v(-2.48, -1.26) * mm});
            skLineSegment(sketch, "E330", {"start": v(-2.48, -1.26) * mm, "end": v(-2.47, -1.2) * mm});
            skLineSegment(sketch, "E331", {"start": v(-2.47, -1.2) * mm, "end": v(-2.46, -1.14) * mm});
            skLineSegment(sketch, "E332", {"start": v(-2.46, -1.14) * mm, "end": v(-2.45, -1.08) * mm});
            skLineSegment(sketch, "E333", {"start": v(-2.45, -1.08) * mm, "end": v(-2.45, -1.01) * mm});
            skLineSegment(sketch, "E334", {"start": v(-2.45, -1.01) * mm, "end": v(-2.45, -0.85) * mm});
            skLineSegment(sketch, "E335", {"start": v(-2.45, -0.85) * mm, "end": v(-2.45, -0.68) * mm});
            skLineSegment(sketch, "E336", {"start": v(-2.45, -0.68) * mm, "end": v(-2.45, -0.52) * mm});
            skLineSegment(sketch, "E337", {"start": v(-2.45, -0.52) * mm, "end": v(-2.45, -0.36) * mm});
            skLineSegment(sketch, "E338", {"start": v(-2.45, -0.36) * mm, "end": v(-2.45, -0.2) * mm});
            skLineSegment(sketch, "E339", {"start": v(-2.45, -0.2) * mm, "end": v(-2.45, -0.03) * mm});
            skLineSegment(sketch, "E340", {"start": v(-2.45, -0.03) * mm, "end": v(-2.45, 0.13) * mm});
            skLineSegment(sketch, "E341", {"start": v(-2.45, 0.13) * mm, "end": v(-2.45, 0.3) * mm});
            skLineSegment(sketch, "E342", {"start": v(-2.45, 0.3) * mm, "end": v(-2.45, 0.46) * mm});
            skLineSegment(sketch, "E343", {"start": v(-2.45, 0.46) * mm, "end": v(-2.45, 0.62) * mm});
            skLineSegment(sketch, "E344", {"start": v(-2.45, 0.62) * mm, "end": v(-2.45, 0.79) * mm});
            skLineSegment(sketch, "E345", {"start": v(-2.45, 0.79) * mm, "end": v(-2.45, 0.95) * mm});
            skLineSegment(sketch, "E346", {"start": v(-2.45, 0.95) * mm, "end": v(-2.45, 1.12) * mm});
            skLineSegment(sketch, "E347", {"start": v(-2.45, 1.12) * mm, "end": v(-2.45, 1.28) * mm});
            skLineSegment(sketch, "E348", {"start": v(-2.45, 1.28) * mm, "end": v(-2.45, 1.44) * mm});
            skLineSegment(sketch, "E349", {"start": v(-2.45, 1.44) * mm, "end": v(-2.45, 1.6) * mm});
            skLineSegment(sketch, "E350", {"start": v(-2.45, 1.6) * mm, "end": v(-2.45, 1.66) * mm});
            skLineSegment(sketch, "E351", {"start": v(-2.45, 1.66) * mm, "end": v(-2.46, 1.71) * mm});
            skLineSegment(sketch, "E352", {"start": v(6.62, 1.66) * mm, "end": v(6.62, 1.71) * mm});
            skLineSegment(sketch, "E353", {"start": v(6.62, 1.71) * mm, "end": v(6.6, 1.76) * mm});
            skLineSegment(sketch, "E354", {"start": v(6.6, 1.76) * mm, "end": v(6.58, 1.81) * mm});
            skLineSegment(sketch, "E355", {"start": v(6.58, 1.81) * mm, "end": v(6.56, 1.86) * mm});
            skLineSegment(sketch, "E356", {"start": v(6.56, 1.86) * mm, "end": v(6.54, 1.9) * mm});
            skLineSegment(sketch, "E357", {"start": v(6.54, 1.9) * mm, "end": v(6.5, 1.94) * mm});
            skLineSegment(sketch, "E358", {"start": v(6.5, 1.94) * mm, "end": v(6.47, 1.98) * mm});
            skLineSegment(sketch, "E359", {"start": v(6.47, 1.98) * mm, "end": v(6.43, 2.01) * mm});
            skLineSegment(sketch, "E360", {"start": v(6.43, 2.01) * mm, "end": v(6.4, 2.05) * mm});
            skLineSegment(sketch, "E361", {"start": v(6.4, 2.05) * mm, "end": v(6.35, 2.07) * mm});
            skLineSegment(sketch, "E362", {"start": v(6.35, 2.07) * mm, "end": v(6.3, 2.1) * mm});
            skLineSegment(sketch, "E363", {"start": v(6.3, 2.1) * mm, "end": v(6.25, 2.11) * mm});
            skLineSegment(sketch, "E364", {"start": v(6.25, 2.11) * mm, "end": v(6.2, 2.13) * mm});
            skLineSegment(sketch, "E365", {"start": v(6.2, 2.13) * mm, "end": v(6.15, 2.13) * mm});
            skLineSegment(sketch, "E366", {"start": v(6.15, 2.13) * mm, "end": v(6.1, 2.14) * mm});
            skLineSegment(sketch, "E367", {"start": v(6.1, 2.14) * mm, "end": v(6.04, 2.13) * mm});
            skLineSegment(sketch, "E368", {"start": v(6.04, 2.13) * mm, "end": v(5.99, 2.13) * mm});
            skLineSegment(sketch, "E369", {"start": v(5.99, 2.13) * mm, "end": v(5.94, 2.11) * mm});
            skLineSegment(sketch, "E370", {"start": v(5.94, 2.11) * mm, "end": v(5.9, 2.1) * mm});
            skLineSegment(sketch, "E371", {"start": v(5.9, 2.1) * mm, "end": v(5.84, 2.07) * mm});
            skLineSegment(sketch, "E372", {"start": v(5.84, 2.07) * mm, "end": v(5.8, 2.05) * mm});
            skLineSegment(sketch, "E373", {"start": v(5.8, 2.05) * mm, "end": v(5.76, 2.01) * mm});
            skLineSegment(sketch, "E374", {"start": v(5.76, 2.01) * mm, "end": v(5.72, 1.98) * mm});
            skLineSegment(sketch, "E375", {"start": v(5.72, 1.98) * mm, "end": v(5.69, 1.94) * mm});
            skLineSegment(sketch, "E376", {"start": v(5.69, 1.94) * mm, "end": v(5.66, 1.9) * mm});
            skLineSegment(sketch, "E377", {"start": v(5.66, 1.9) * mm, "end": v(5.63, 1.86) * mm});
            skLineSegment(sketch, "E378", {"start": v(5.63, 1.86) * mm, "end": v(5.6, 1.81) * mm});
            skLineSegment(sketch, "E379", {"start": v(5.6, 1.81) * mm, "end": v(5.6, 1.76) * mm});
            skLineSegment(sketch, "E380", {"start": v(5.6, 1.76) * mm, "end": v(5.58, 1.71) * mm});
            skLineSegment(sketch, "E381", {"start": v(5.58, 1.71) * mm, "end": v(5.57, 1.66) * mm});
            skLineSegment(sketch, "E382", {"start": v(5.57, 1.66) * mm, "end": v(5.57, 1.6) * mm});
            skLineSegment(sketch, "E383", {"start": v(5.57, 1.6) * mm, "end": v(5.57, 1.5) * mm});
            skLineSegment(sketch, "E384", {"start": v(5.57, 1.5) * mm, "end": v(5.57, 1.38) * mm});
            skLineSegment(sketch, "E385", {"start": v(5.57, 1.38) * mm, "end": v(5.57, 1.26) * mm});
            skLineSegment(sketch, "E386", {"start": v(5.57, 1.26) * mm, "end": v(5.57, 1.15) * mm});
            skLineSegment(sketch, "E387", {"start": v(5.57, 1.15) * mm, "end": v(5.57, 1.03) * mm});
            skLineSegment(sketch, "E388", {"start": v(5.57, 1.03) * mm, "end": v(5.57, 0.92) * mm});
            skLineSegment(sketch, "E389", {"start": v(5.57, 0.92) * mm, "end": v(5.57, 0.8) * mm});
            skLineSegment(sketch, "E390", {"start": v(5.57, 0.8) * mm, "end": v(5.57, 0.69) * mm});
            skLineSegment(sketch, "E391", {"start": v(5.57, 0.69) * mm, "end": v(5.57, 0.57) * mm});
            skLineSegment(sketch, "E392", {"start": v(5.57, 0.57) * mm, "end": v(5.57, 0.46) * mm});
            skLineSegment(sketch, "E393", {"start": v(5.57, 0.46) * mm, "end": v(5.57, 0.34) * mm});
            skLineSegment(sketch, "E394", {"start": v(5.57, 0.34) * mm, "end": v(5.57, 0.23) * mm});
            skLineSegment(sketch, "E395", {"start": v(5.57, 0.23) * mm, "end": v(5.57, 0.11) * mm});
            skLineSegment(sketch, "E396", {"start": v(5.57, 0.11) * mm, "end": v(5.57, 0) * mm});
            skLineSegment(sketch, "E397", {"start": v(5.57, 0) * mm, "end": v(5.57, -0.12) * mm});
            skLineSegment(sketch, "E398", {"start": v(5.57, -0.12) * mm, "end": v(5.57, -0.23) * mm});
            skLineSegment(sketch, "E399", {"start": v(5.57, -0.23) * mm, "end": v(5.55, -0.22) * mm});
            skLineSegment(sketch, "E400", {"start": v(5.55, -0.22) * mm, "end": v(5.53, -0.2) * mm});
            skLineSegment(sketch, "E401", {"start": v(5.53, -0.2) * mm, "end": v(5.51, -0.18) * mm});
            skLineSegment(sketch, "E402", {"start": v(5.51, -0.18) * mm, "end": v(5.5, -0.16) * mm});
            skLineSegment(sketch, "E403", {"start": v(5.5, -0.16) * mm, "end": v(5.47, -0.14) * mm});
            skLineSegment(sketch, "E404", {"start": v(5.47, -0.14) * mm, "end": v(5.45, -0.12) * mm});
            skLineSegment(sketch, "E405", {"start": v(5.45, -0.12) * mm, "end": v(5.44, -0.1) * mm});
            skLineSegment(sketch, "E406", {"start": v(5.44, -0.1) * mm, "end": v(5.42, -0.08) * mm});
            skLineSegment(sketch, "E407", {"start": v(5.42, -0.08) * mm, "end": v(5.4, -0.06) * mm});
            skLineSegment(sketch, "E408", {"start": v(5.4, -0.06) * mm, "end": v(5.38, -0.05) * mm});
            skLineSegment(sketch, "E409", {"start": v(5.38, -0.05) * mm, "end": v(5.36, -0.03) * mm});
            skLineSegment(sketch, "E410", {"start": v(5.36, -0.03) * mm, "end": v(5.34, 0) * mm});
            skLineSegment(sketch, "E411", {"start": v(5.34, 0) * mm, "end": v(5.32, 0.01) * mm});
            skLineSegment(sketch, "E412", {"start": v(5.32, 0.01) * mm, "end": v(5.3, 0.03) * mm});
            skLineSegment(sketch, "E413", {"start": v(5.3, 0.03) * mm, "end": v(5.28, 0.05) * mm});
            skLineSegment(sketch, "E414", {"start": v(5.28, 0.05) * mm, "end": v(5.27, 0.07) * mm});
            skLineSegment(sketch, "E415", {"start": v(5.27, 0.07) * mm, "end": v(5.19, 0.14) * mm});
            skLineSegment(sketch, "E416", {"start": v(5.19, 0.14) * mm, "end": v(5.1, 0.2) * mm});
            skLineSegment(sketch, "E417", {"start": v(5.1, 0.2) * mm, "end": v(5.02, 0.25) * mm});
            skLineSegment(sketch, "E418", {"start": v(5.02, 0.25) * mm, "end": v(4.92, 0.3) * mm});
            skLineSegment(sketch, "E419", {"start": v(4.92, 0.3) * mm, "end": v(4.83, 0.33) * mm});
            skLineSegment(sketch, "E420", {"start": v(4.83, 0.33) * mm, "end": v(4.73, 0.35) * mm});
            skLineSegment(sketch, "E421", {"start": v(4.73, 0.35) * mm, "end": v(4.64, 0.36) * mm});
            skLineSegment(sketch, "E422", {"start": v(4.64, 0.36) * mm, "end": v(4.54, 0.37) * mm});
            skLineSegment(sketch, "E423", {"start": v(4.54, 0.37) * mm, "end": v(4.44, 0.36) * mm});
            skLineSegment(sketch, "E424", {"start": v(4.44, 0.36) * mm, "end": v(4.34, 0.35) * mm});
            skLineSegment(sketch, "E425", {"start": v(4.34, 0.35) * mm, "end": v(4.24, 0.33) * mm});
            skLineSegment(sketch, "E426", {"start": v(4.24, 0.33) * mm, "end": v(4.15, 0.3) * mm});
            skLineSegment(sketch, "E427", {"start": v(4.15, 0.3) * mm, "end": v(4.06, 0.25) * mm});
            skLineSegment(sketch, "E428", {"start": v(4.06, 0.25) * mm, "end": v(3.97, 0.2) * mm});
            skLineSegment(sketch, "E429", {"start": v(3.97, 0.2) * mm, "end": v(3.89, 0.14) * mm});
            skLineSegment(sketch, "E430", {"start": v(3.89, 0.14) * mm, "end": v(3.8, 0.07) * mm});
            skLineSegment(sketch, "E431", {"start": v(3.8, 0.07) * mm, "end": v(3.8, 0.05) * mm});
            skLineSegment(sketch, "E432", {"start": v(3.8, 0.05) * mm, "end": v(3.77, 0.03) * mm});
            skLineSegment(sketch, "E433", {"start": v(3.77, 0.03) * mm, "end": v(3.75, 0.01) * mm});
            skLineSegment(sketch, "E434", {"start": v(3.75, 0.01) * mm, "end": v(3.73, 0) * mm});
            skLineSegment(sketch, "E435", {"start": v(3.73, 0) * mm, "end": v(3.72, -0.03) * mm});
            skLineSegment(sketch, "E436", {"start": v(3.72, -0.03) * mm, "end": v(3.7, -0.05) * mm});
            skLineSegment(sketch, "E437", {"start": v(3.7, -0.05) * mm, "end": v(3.68, -0.06) * mm});
            skLineSegment(sketch, "E438", {"start": v(3.68, -0.06) * mm, "end": v(3.66, -0.08) * mm});
            skLineSegment(sketch, "E439", {"start": v(3.66, -0.08) * mm, "end": v(3.64, -0.1) * mm});
            skLineSegment(sketch, "E440", {"start": v(3.64, -0.1) * mm, "end": v(3.62, -0.12) * mm});
            skLineSegment(sketch, "E441", {"start": v(3.62, -0.12) * mm, "end": v(3.6, -0.14) * mm});
            skLineSegment(sketch, "E442", {"start": v(3.6, -0.14) * mm, "end": v(3.58, -0.16) * mm});
            skLineSegment(sketch, "E443", {"start": v(3.58, -0.16) * mm, "end": v(3.56, -0.18) * mm});
            skLineSegment(sketch, "E444", {"start": v(3.56, -0.18) * mm, "end": v(3.55, -0.2) * mm});
            skLineSegment(sketch, "E445", {"start": v(3.55, -0.2) * mm, "end": v(3.53, -0.22) * mm});
            skLineSegment(sketch, "E446", {"start": v(3.53, -0.22) * mm, "end": v(3.5, -0.23) * mm});
            skLineSegment(sketch, "E447", {"start": v(3.5, -0.23) * mm, "end": v(3.5, -0.12) * mm});
            skLineSegment(sketch, "E448", {"start": v(3.5, -0.12) * mm, "end": v(3.5, 0) * mm});
            skLineSegment(sketch, "E449", {"start": v(3.5, 0) * mm, "end": v(3.5, 0.11) * mm});
            skLineSegment(sketch, "E450", {"start": v(3.5, 0.11) * mm, "end": v(3.5, 0.23) * mm});
            skLineSegment(sketch, "E451", {"start": v(3.5, 0.23) * mm, "end": v(3.5, 0.34) * mm});
            skLineSegment(sketch, "E452", {"start": v(3.5, 0.34) * mm, "end": v(3.5, 0.46) * mm});
            skLineSegment(sketch, "E453", {"start": v(3.5, 0.46) * mm, "end": v(3.5, 0.57) * mm});
            skLineSegment(sketch, "E454", {"start": v(3.5, 0.57) * mm, "end": v(3.5, 0.69) * mm});
            skLineSegment(sketch, "E455", {"start": v(3.5, 0.69) * mm, "end": v(3.5, 0.8) * mm});
            skLineSegment(sketch, "E456", {"start": v(3.5, 0.8) * mm, "end": v(3.5, 0.92) * mm});
            skLineSegment(sketch, "E457", {"start": v(3.5, 0.92) * mm, "end": v(3.5, 1.03) * mm});
            skLineSegment(sketch, "E458", {"start": v(3.5, 1.03) * mm, "end": v(3.5, 1.15) * mm});
            skLineSegment(sketch, "E459", {"start": v(3.5, 1.15) * mm, "end": v(3.5, 1.26) * mm});
            skLineSegment(sketch, "E460", {"start": v(3.5, 1.26) * mm, "end": v(3.5, 1.38) * mm});
            skLineSegment(sketch, "E461", {"start": v(3.5, 1.38) * mm, "end": v(3.5, 1.5) * mm});
            skLineSegment(sketch, "E462", {"start": v(3.5, 1.5) * mm, "end": v(3.5, 1.6) * mm});
            skLineSegment(sketch, "E463", {"start": v(3.5, 1.6) * mm, "end": v(3.5, 1.66) * mm});
            skLineSegment(sketch, "E464", {"start": v(3.5, 1.66) * mm, "end": v(3.5, 1.71) * mm});
            skLineSegment(sketch, "E465", {"start": v(3.5, 1.71) * mm, "end": v(3.48, 1.76) * mm});
            skLineSegment(sketch, "E466", {"start": v(3.48, 1.76) * mm, "end": v(3.47, 1.81) * mm});
            skLineSegment(sketch, "E467", {"start": v(3.47, 1.81) * mm, "end": v(3.44, 1.86) * mm});
            skLineSegment(sketch, "E468", {"start": v(3.44, 1.86) * mm, "end": v(3.42, 1.9) * mm});
            skLineSegment(sketch, "E469", {"start": v(3.42, 1.9) * mm, "end": v(3.39, 1.94) * mm});
            skLineSegment(sketch, "E470", {"start": v(3.39, 1.94) * mm, "end": v(3.35, 1.98) * mm});
            skLineSegment(sketch, "E471", {"start": v(3.35, 1.98) * mm, "end": v(3.31, 2.01) * mm});
            skLineSegment(sketch, "E472", {"start": v(3.31, 2.01) * mm, "end": v(3.27, 2.05) * mm});
            skLineSegment(sketch, "E473", {"start": v(3.27, 2.05) * mm, "end": v(3.23, 2.07) * mm});
            skLineSegment(sketch, "E474", {"start": v(3.23, 2.07) * mm, "end": v(3.18, 2.1) * mm});
            skLineSegment(sketch, "E475", {"start": v(3.18, 2.1) * mm, "end": v(3.14, 2.11) * mm});
            skLineSegment(sketch, "E476", {"start": v(3.14, 2.11) * mm, "end": v(3.09, 2.13) * mm});
            skLineSegment(sketch, "E477", {"start": v(3.09, 2.13) * mm, "end": v(3.03, 2.13) * mm});
            skLineSegment(sketch, "E478", {"start": v(3.03, 2.13) * mm, "end": v(2.98, 2.14) * mm});
            skLineSegment(sketch, "E479", {"start": v(2.98, 2.14) * mm, "end": v(2.92, 2.13) * mm});
            skLineSegment(sketch, "E480", {"start": v(2.92, 2.13) * mm, "end": v(2.87, 2.13) * mm});
            skLineSegment(sketch, "E481", {"start": v(2.87, 2.13) * mm, "end": v(2.82, 2.11) * mm});
            skLineSegment(sketch, "E482", {"start": v(2.82, 2.11) * mm, "end": v(2.77, 2.1) * mm});
            skLineSegment(sketch, "E483", {"start": v(2.77, 2.1) * mm, "end": v(2.73, 2.07) * mm});
            skLineSegment(sketch, "E484", {"start": v(2.73, 2.07) * mm, "end": v(2.68, 2.05) * mm});
            skLineSegment(sketch, "E485", {"start": v(2.68, 2.05) * mm, "end": v(2.64, 2.01) * mm});
            skLineSegment(sketch, "E486", {"start": v(2.64, 2.01) * mm, "end": v(2.6, 1.98) * mm});
            skLineSegment(sketch, "E487", {"start": v(2.6, 1.98) * mm, "end": v(2.57, 1.94) * mm});
            skLineSegment(sketch, "E488", {"start": v(2.57, 1.94) * mm, "end": v(2.54, 1.9) * mm});
            skLineSegment(sketch, "E489", {"start": v(2.54, 1.9) * mm, "end": v(2.51, 1.86) * mm});
            skLineSegment(sketch, "E490", {"start": v(2.51, 1.86) * mm, "end": v(2.5, 1.81) * mm});
            skLineSegment(sketch, "E491", {"start": v(2.5, 1.81) * mm, "end": v(2.47, 1.76) * mm});
            skLineSegment(sketch, "E492", {"start": v(2.47, 1.76) * mm, "end": v(2.46, 1.71) * mm});
            skLineSegment(sketch, "E493", {"start": v(2.46, 1.71) * mm, "end": v(2.45, 1.66) * mm});
            skLineSegment(sketch, "E494", {"start": v(2.45, 1.66) * mm, "end": v(2.45, 1.6) * mm});
            skLineSegment(sketch, "E495", {"start": v(2.45, 1.6) * mm, "end": v(2.45, 1.44) * mm});
            skLineSegment(sketch, "E496", {"start": v(2.45, 1.44) * mm, "end": v(2.45, 1.28) * mm});
            skLineSegment(sketch, "E497", {"start": v(2.45, 1.28) * mm, "end": v(2.45, 1.12) * mm});
            skLineSegment(sketch, "E498", {"start": v(2.45, 1.12) * mm, "end": v(2.45, 0.95) * mm});
            skLineSegment(sketch, "E499", {"start": v(2.45, 0.95) * mm, "end": v(2.45, 0.79) * mm});
            skLineSegment(sketch, "E500", {"start": v(2.45, 0.79) * mm, "end": v(2.45, 0.62) * mm});
            skLineSegment(sketch, "E501", {"start": v(2.45, 0.62) * mm, "end": v(2.45, 0.46) * mm});
            skLineSegment(sketch, "E502", {"start": v(2.45, 0.46) * mm, "end": v(2.45, 0.3) * mm});
            skLineSegment(sketch, "E503", {"start": v(2.45, 0.3) * mm, "end": v(2.45, 0.13) * mm});
            skLineSegment(sketch, "E504", {"start": v(2.45, 0.13) * mm, "end": v(2.45, -0.03) * mm});
            skLineSegment(sketch, "E505", {"start": v(2.45, -0.03) * mm, "end": v(2.45, -0.2) * mm});
            skLineSegment(sketch, "E506", {"start": v(2.45, -0.2) * mm, "end": v(2.45, -0.36) * mm});
            skLineSegment(sketch, "E507", {"start": v(2.45, -0.36) * mm, "end": v(2.45, -0.52) * mm});
            skLineSegment(sketch, "E508", {"start": v(2.45, -0.52) * mm, "end": v(2.45, -0.68) * mm});
            skLineSegment(sketch, "E509", {"start": v(2.45, -0.68) * mm, "end": v(2.45, -0.85) * mm});
            skLineSegment(sketch, "E510", {"start": v(2.45, -0.85) * mm, "end": v(2.45, -1.01) * mm});
            skLineSegment(sketch, "E511", {"start": v(2.45, -1.01) * mm, "end": v(2.45, -1.08) * mm});
            skLineSegment(sketch, "E512", {"start": v(2.45, -1.08) * mm, "end": v(2.46, -1.14) * mm});
            skLineSegment(sketch, "E513", {"start": v(2.46, -1.14) * mm, "end": v(2.47, -1.2) * mm});
            skLineSegment(sketch, "E514", {"start": v(2.47, -1.2) * mm, "end": v(2.48, -1.26) * mm});
            skLineSegment(sketch, "E515", {"start": v(2.48, -1.26) * mm, "end": v(2.5, -1.32) * mm});
            skLineSegment(sketch, "E516", {"start": v(2.5, -1.32) * mm, "end": v(2.51, -1.37) * mm});
            skLineSegment(sketch, "E517", {"start": v(2.51, -1.37) * mm, "end": v(2.54, -1.42) * mm});
            skLineSegment(sketch, "E518", {"start": v(2.54, -1.42) * mm, "end": v(2.56, -1.47) * mm});
            skLineSegment(sketch, "E519", {"start": v(2.56, -1.47) * mm, "end": v(2.6, -1.52) * mm});
            skLineSegment(sketch, "E520", {"start": v(2.6, -1.52) * mm, "end": v(2.62, -1.56) * mm});
            skLineSegment(sketch, "E521", {"start": v(2.62, -1.56) * mm, "end": v(2.66, -1.6) * mm});
            skLineSegment(sketch, "E522", {"start": v(2.66, -1.6) * mm, "end": v(2.7, -1.64) * mm});
            skLineSegment(sketch, "E523", {"start": v(2.7, -1.64) * mm, "end": v(2.74, -1.67) * mm});
            skLineSegment(sketch, "E524", {"start": v(2.74, -1.67) * mm, "end": v(2.78, -1.7) * mm});
            skLineSegment(sketch, "E525", {"start": v(2.78, -1.7) * mm, "end": v(2.83, -1.73) * mm});
            skLineSegment(sketch, "E526", {"start": v(2.83, -1.73) * mm, "end": v(2.88, -1.75) * mm});
            skLineSegment(sketch, "E527", {"start": v(2.88, -1.75) * mm, "end": v(2.93, -1.77) * mm});
            skLineSegment(sketch, "E528", {"start": v(2.93, -1.77) * mm, "end": v(2.98, -1.78) * mm});
            skLineSegment(sketch, "E529", {"start": v(2.98, -1.78) * mm, "end": v(3.03, -1.8) * mm});
            skLineSegment(sketch, "E530", {"start": v(3.03, -1.8) * mm, "end": v(3.09, -1.8) * mm});
            skLineSegment(sketch, "E531", {"start": v(3.09, -1.8) * mm, "end": v(3.14, -1.8) * mm});
            skLineSegment(sketch, "E532", {"start": v(3.14, -1.8) * mm, "end": v(3.2, -1.8) * mm});
            skLineSegment(sketch, "E533", {"start": v(3.2, -1.8) * mm, "end": v(3.25, -1.79) * mm});
            skLineSegment(sketch, "E534", {"start": v(3.25, -1.79) * mm, "end": v(3.3, -1.78) * mm});
            skLineSegment(sketch, "E535", {"start": v(3.3, -1.78) * mm, "end": v(3.35, -1.76) * mm});
            skLineSegment(sketch, "E536", {"start": v(3.35, -1.76) * mm, "end": v(3.4, -1.74) * mm});
            skLineSegment(sketch, "E537", {"start": v(3.4, -1.74) * mm, "end": v(3.46, -1.72) * mm});
            skLineSegment(sketch, "E538", {"start": v(3.46, -1.72) * mm, "end": v(3.51, -1.69) * mm});
            skLineSegment(sketch, "E539", {"start": v(3.51, -1.69) * mm, "end": v(3.56, -1.65) * mm});
            skLineSegment(sketch, "E540", {"start": v(3.56, -1.65) * mm, "end": v(3.61, -1.62) * mm});
            skLineSegment(sketch, "E541", {"start": v(3.61, -1.62) * mm, "end": v(3.66, -1.58) * mm});
            skLineSegment(sketch, "E542", {"start": v(3.66, -1.58) * mm, "end": v(3.7, -1.53) * mm});
            skLineSegment(sketch, "E543", {"start": v(3.7, -1.53) * mm, "end": v(3.76, -1.48) * mm});
            skLineSegment(sketch, "E544", {"start": v(3.76, -1.48) * mm, "end": v(3.8, -1.43) * mm});
            skLineSegment(sketch, "E545", {"start": v(3.8, -1.43) * mm, "end": v(3.86, -1.38) * mm});
            skLineSegment(sketch, "E546", {"start": v(3.86, -1.38) * mm, "end": v(3.91, -1.32) * mm});
            skLineSegment(sketch, "E547", {"start": v(3.91, -1.32) * mm, "end": v(3.97, -1.27) * mm});
            skLineSegment(sketch, "E548", {"start": v(3.97, -1.27) * mm, "end": v(4.02, -1.22) * mm});
            skLineSegment(sketch, "E549", {"start": v(4.02, -1.22) * mm, "end": v(4.07, -1.17) * mm});
            skLineSegment(sketch, "E550", {"start": v(4.07, -1.17) * mm, "end": v(4.12, -1.12) * mm});
            skLineSegment(sketch, "E551", {"start": v(4.12, -1.12) * mm, "end": v(4.17, -1.06) * mm});
            skLineSegment(sketch, "E552", {"start": v(4.17, -1.06) * mm, "end": v(4.23, -1.01) * mm});
            skLineSegment(sketch, "E553", {"start": v(4.23, -1.01) * mm, "end": v(4.28, -0.96) * mm});
            skLineSegment(sketch, "E554", {"start": v(4.28, -0.96) * mm, "end": v(4.33, -0.9) * mm});
            skLineSegment(sketch, "E555", {"start": v(4.33, -0.9) * mm, "end": v(4.38, -0.86) * mm});
            skLineSegment(sketch, "E556", {"start": v(4.38, -0.86) * mm, "end": v(4.43, -0.8) * mm});
            skLineSegment(sketch, "E557", {"start": v(4.43, -0.8) * mm, "end": v(4.49, -0.75) * mm});
            skLineSegment(sketch, "E558", {"start": v(4.49, -0.75) * mm, "end": v(4.54, -0.7) * mm});
            skLineSegment(sketch, "E559", {"start": v(4.54, -0.7) * mm, "end": v(4.59, -0.75) * mm});
            skLineSegment(sketch, "E560", {"start": v(4.59, -0.75) * mm, "end": v(4.64, -0.8) * mm});
            skLineSegment(sketch, "E561", {"start": v(4.64, -0.8) * mm, "end": v(4.7, -0.86) * mm});
            skLineSegment(sketch, "E562", {"start": v(4.7, -0.86) * mm, "end": v(4.75, -0.9) * mm});
            skLineSegment(sketch, "E563", {"start": v(4.75, -0.9) * mm, "end": v(4.8, -0.96) * mm});
            skLineSegment(sketch, "E564", {"start": v(4.8, -0.96) * mm, "end": v(4.85, -1.01) * mm});
            skLineSegment(sketch, "E565", {"start": v(4.85, -1.01) * mm, "end": v(4.9, -1.06) * mm});
            skLineSegment(sketch, "E566", {"start": v(4.9, -1.06) * mm, "end": v(4.95, -1.12) * mm});
            skLineSegment(sketch, "E567", {"start": v(4.95, -1.12) * mm, "end": v(5, -1.17) * mm});
            skLineSegment(sketch, "E568", {"start": v(5, -1.17) * mm, "end": v(5.06, -1.22) * mm});
            skLineSegment(sketch, "E569", {"start": v(5.06, -1.22) * mm, "end": v(5.1, -1.27) * mm});
            skLineSegment(sketch, "E570", {"start": v(5.1, -1.27) * mm, "end": v(5.16, -1.32) * mm});
            skLineSegment(sketch, "E571", {"start": v(5.16, -1.32) * mm, "end": v(5.21, -1.38) * mm});
            skLineSegment(sketch, "E572", {"start": v(5.21, -1.38) * mm, "end": v(5.27, -1.43) * mm});
            skLineSegment(sketch, "E573", {"start": v(5.27, -1.43) * mm, "end": v(5.32, -1.48) * mm});
            skLineSegment(sketch, "E574", {"start": v(5.32, -1.48) * mm, "end": v(5.37, -1.53) * mm});
            skLineSegment(sketch, "E575", {"start": v(5.37, -1.53) * mm, "end": v(5.4, -1.56) * mm});
            skLineSegment(sketch, "E576", {"start": v(5.4, -1.56) * mm, "end": v(5.44, -1.6) * mm});
            skLineSegment(sketch, "E577", {"start": v(5.44, -1.6) * mm, "end": v(5.47, -1.62) * mm});
            skLineSegment(sketch, "E578", {"start": v(5.47, -1.62) * mm, "end": v(5.5, -1.65) * mm});
            skLineSegment(sketch, "E579", {"start": v(5.5, -1.65) * mm, "end": v(5.54, -1.67) * mm});
            skLineSegment(sketch, "E580", {"start": v(5.54, -1.67) * mm, "end": v(5.58, -1.7) * mm});
            skLineSegment(sketch, "E581", {"start": v(5.58, -1.7) * mm, "end": v(5.61, -1.71) * mm});
            skLineSegment(sketch, "E582", {"start": v(5.61, -1.71) * mm, "end": v(5.65, -1.73) * mm});
            skLineSegment(sketch, "E583", {"start": v(5.65, -1.73) * mm, "end": v(5.69, -1.75) * mm});
            skLineSegment(sketch, "E584", {"start": v(5.69, -1.75) * mm, "end": v(5.72, -1.76) * mm});
            skLineSegment(sketch, "E585", {"start": v(5.72, -1.76) * mm, "end": v(5.76, -1.77) * mm});
            skLineSegment(sketch, "E586", {"start": v(5.76, -1.77) * mm, "end": v(5.8, -1.78) * mm});
            skLineSegment(sketch, "E587", {"start": v(5.8, -1.78) * mm, "end": v(5.84, -1.79) * mm});
            skLineSegment(sketch, "E588", {"start": v(5.84, -1.79) * mm, "end": v(5.87, -1.8) * mm});
            skLineSegment(sketch, "E589", {"start": v(5.87, -1.8) * mm, "end": v(5.91, -1.8) * mm});
            skLineSegment(sketch, "E590", {"start": v(5.91, -1.8) * mm, "end": v(5.95, -1.8) * mm});
            skLineSegment(sketch, "E591", {"start": v(5.95, -1.8) * mm, "end": v(5.96, -1.8) * mm});
            skLineSegment(sketch, "E592", {"start": v(5.96, -1.8) * mm, "end": v(5.98, -1.8) * mm});
            skLineSegment(sketch, "E593", {"start": v(5.98, -1.8) * mm, "end": v(6, -1.8) * mm});
            skLineSegment(sketch, "E594", {"start": v(6, -1.8) * mm, "end": v(6.01, -1.8) * mm});
            skLineSegment(sketch, "E595", {"start": v(6.01, -1.8) * mm, "end": v(6.03, -1.8) * mm});
            skLineSegment(sketch, "E596", {"start": v(6.03, -1.8) * mm, "end": v(6.04, -1.8) * mm});
            skLineSegment(sketch, "E597", {"start": v(6.04, -1.8) * mm, "end": v(6.06, -1.79) * mm});
            skLineSegment(sketch, "E598", {"start": v(6.06, -1.79) * mm, "end": v(6.07, -1.79) * mm});
            skLineSegment(sketch, "E599", {"start": v(6.07, -1.79) * mm, "end": v(6.09, -1.78) * mm});
            skLineSegment(sketch, "E600", {"start": v(6.09, -1.78) * mm, "end": v(6.1, -1.78) * mm});
            skLineSegment(sketch, "E601", {"start": v(6.1, -1.78) * mm, "end": v(6.12, -1.78) * mm});
            skLineSegment(sketch, "E602", {"start": v(6.12, -1.78) * mm, "end": v(6.14, -1.77) * mm});
            skLineSegment(sketch, "E603", {"start": v(6.14, -1.77) * mm, "end": v(6.15, -1.77) * mm});
            skLineSegment(sketch, "E604", {"start": v(6.15, -1.77) * mm, "end": v(6.17, -1.76) * mm});
            skLineSegment(sketch, "E605", {"start": v(6.17, -1.76) * mm, "end": v(6.18, -1.76) * mm});
            skLineSegment(sketch, "E606", {"start": v(6.18, -1.76) * mm, "end": v(6.2, -1.75) * mm});
            skLineSegment(sketch, "E607", {"start": v(6.2, -1.75) * mm, "end": v(6.24, -1.73) * mm});
            skLineSegment(sketch, "E608", {"start": v(6.24, -1.73) * mm, "end": v(6.3, -1.7) * mm});
            skLineSegment(sketch, "E609", {"start": v(6.3, -1.7) * mm, "end": v(6.34, -1.67) * mm});
            skLineSegment(sketch, "E610", {"start": v(6.34, -1.67) * mm, "end": v(6.38, -1.64) * mm});
            skLineSegment(sketch, "E611", {"start": v(6.38, -1.64) * mm, "end": v(6.41, -1.6) * mm});
            skLineSegment(sketch, "E612", {"start": v(6.41, -1.6) * mm, "end": v(6.45, -1.56) * mm});
            skLineSegment(sketch, "E613", {"start": v(6.45, -1.56) * mm, "end": v(6.48, -1.52) * mm});
            skLineSegment(sketch, "E614", {"start": v(6.48, -1.52) * mm, "end": v(6.51, -1.47) * mm});
            skLineSegment(sketch, "E615", {"start": v(6.51, -1.47) * mm, "end": v(6.54, -1.42) * mm});
            skLineSegment(sketch, "E616", {"start": v(6.54, -1.42) * mm, "end": v(6.56, -1.37) * mm});
            skLineSegment(sketch, "E617", {"start": v(6.56, -1.37) * mm, "end": v(6.58, -1.32) * mm});
            skLineSegment(sketch, "E618", {"start": v(6.58, -1.32) * mm, "end": v(6.6, -1.26) * mm});
            skLineSegment(sketch, "E619", {"start": v(6.6, -1.26) * mm, "end": v(6.6, -1.2) * mm});
            skLineSegment(sketch, "E620", {"start": v(6.6, -1.2) * mm, "end": v(6.62, -1.14) * mm});
            skLineSegment(sketch, "E621", {"start": v(6.62, -1.14) * mm, "end": v(6.62, -1.08) * mm});
            skLineSegment(sketch, "E622", {"start": v(6.62, -1.08) * mm, "end": v(6.63, -1.01) * mm});
            skLineSegment(sketch, "E623", {"start": v(6.63, -1.01) * mm, "end": v(6.63, -0.85) * mm});
            skLineSegment(sketch, "E624", {"start": v(6.63, -0.85) * mm, "end": v(6.63, -0.68) * mm});
            skLineSegment(sketch, "E625", {"start": v(6.63, -0.68) * mm, "end": v(6.63, -0.52) * mm});
            skLineSegment(sketch, "E626", {"start": v(6.63, -0.52) * mm, "end": v(6.63, -0.36) * mm});
            skLineSegment(sketch, "E627", {"start": v(6.63, -0.36) * mm, "end": v(6.63, -0.2) * mm});
            skLineSegment(sketch, "E628", {"start": v(6.63, -0.2) * mm, "end": v(6.63, -0.03) * mm});
            skLineSegment(sketch, "E629", {"start": v(6.63, -0.03) * mm, "end": v(6.63, 0.13) * mm});
            skLineSegment(sketch, "E630", {"start": v(6.63, 0.13) * mm, "end": v(6.63, 0.3) * mm});
            skLineSegment(sketch, "E631", {"start": v(6.63, 0.3) * mm, "end": v(6.63, 0.46) * mm});
            skLineSegment(sketch, "E632", {"start": v(6.63, 0.46) * mm, "end": v(6.63, 0.62) * mm});
            skLineSegment(sketch, "E633", {"start": v(6.63, 0.62) * mm, "end": v(6.63, 0.79) * mm});
            skLineSegment(sketch, "E634", {"start": v(6.63, 0.79) * mm, "end": v(6.63, 0.95) * mm});
            skLineSegment(sketch, "E635", {"start": v(6.63, 0.95) * mm, "end": v(6.63, 1.12) * mm});
            skLineSegment(sketch, "E636", {"start": v(6.63, 1.12) * mm, "end": v(6.63, 1.28) * mm});
            skLineSegment(sketch, "E637", {"start": v(6.63, 1.28) * mm, "end": v(6.63, 1.44) * mm});
            skLineSegment(sketch, "E638", {"start": v(6.63, 1.44) * mm, "end": v(6.63, 1.6) * mm});
            skLineSegment(sketch, "E639", {"start": v(6.63, 1.6) * mm, "end": v(6.62, 1.66) * mm});
            skSolve(sketch);
        }
        {
            var Q0;
            Q0=qSketchRegion(id+"F0",true);
            extrude(context, id + "F1", {"entities" : qUnion([Q0]), "depth" : 1 * mm});
        }
    });
